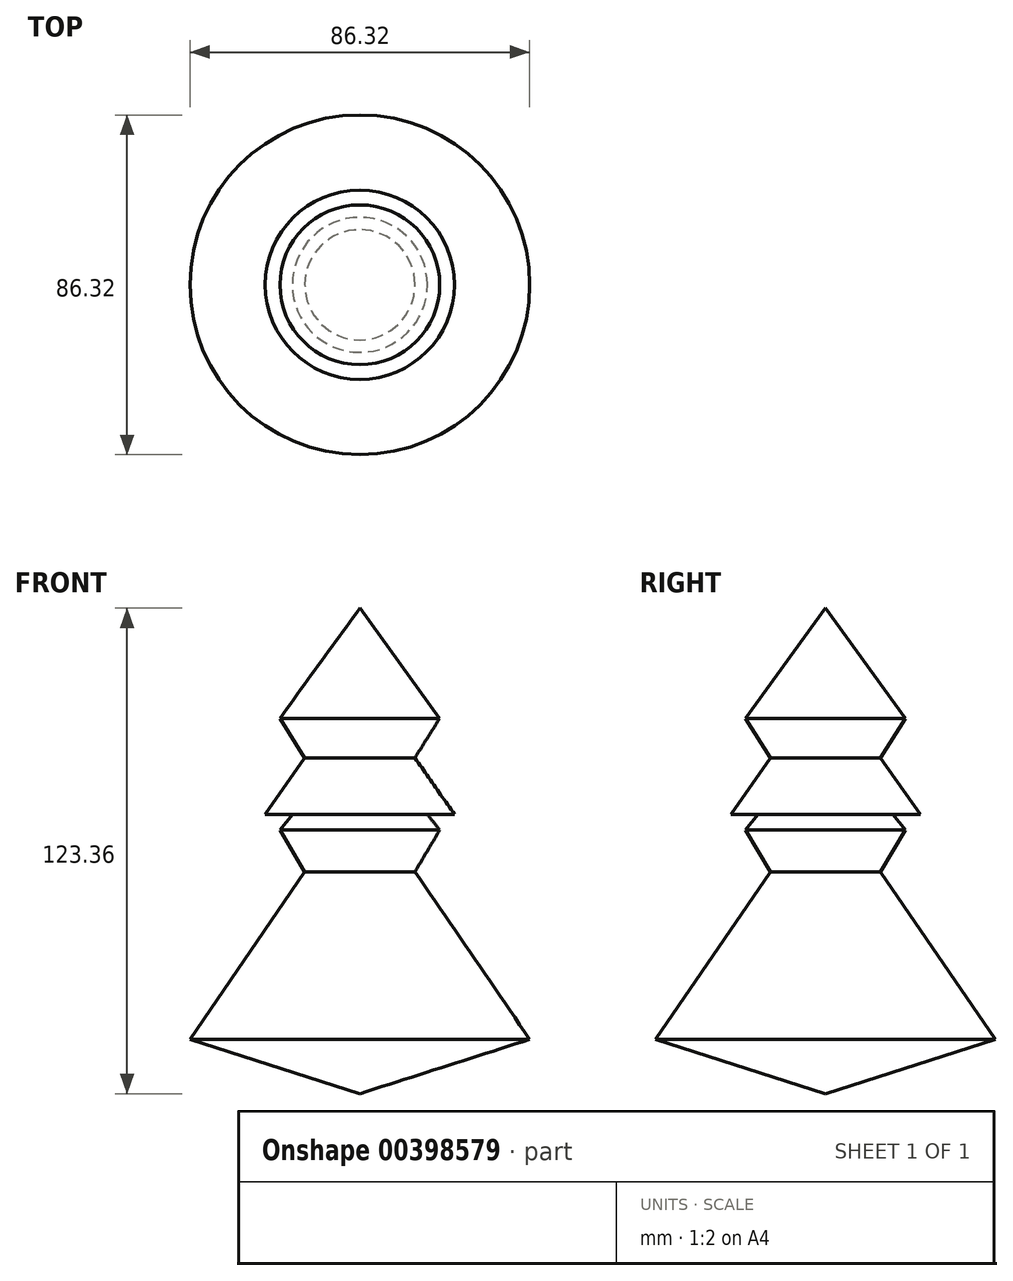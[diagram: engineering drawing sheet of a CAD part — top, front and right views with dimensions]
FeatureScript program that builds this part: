
annotation { "Feature Type Name" : "Feature", "Feature Type Description" : "" }
export const myFeature = defineFeature(function(context is Context, id is Id, definition is map)
    precondition{}
    {
        {
            var Q0;
            Q0=qCreatedBy(makeId("Front.planeOp"),FACE);
            var sketch = newSketch(context, id + "F0", { "sketchPlane" : qUnion([Q0])});
            skLineSegment(sketch, "E0", {"start": v(-50.25, 56.36) * mm, "end": v(-50.25, -67) * mm});
            skLineSegment(sketch, "E1", {"start": v(-50.25, 56.36) * mm, "end": v(-29.95, 28.38) * mm});
            skLineSegment(sketch, "E2", {"start": v(-29.95, 28.38) * mm, "end": v(-36.26, 18.33) * mm});
            skLineSegment(sketch, "E3", {"start": v(-36.26, 18.33) * mm, "end": v(-26.21, 3.94) * mm});
            skLineSegment(sketch, "E4", {"start": v(-26.21, 3.94) * mm, "end": v(-33.1, 3.94) * mm});
            skLineSegment(sketch, "E5", {"start": v(-33.1, 3.94) * mm, "end": v(-29.95, 0) * mm});
            skLineSegment(sketch, "E6", {"start": v(-29.95, 0) * mm, "end": v(-36.26, -10.64) * mm});
            skLineSegment(sketch, "E7", {"start": v(-36.26, -10.64) * mm, "end": v(-7.1, -53.2) * mm});
            skLineSegment(sketch, "E8", {"start": v(-7.1, -53.2) * mm, "end": v(-50.25, -67) * mm});
            skSolve(sketch);
        }
        {
            var Q0;
            Q0=makeQuery(id+"F0.imprint","IMPRINT",FACE,{"disambiguationData":[TD([[makeQuery(id+"F0.imprint","IMPRINT",EDGE,{"derivedFrom":sQuery(id+"F0.wireOp",EDGE,"E0")}),1.0]])]});
            var Q1;
            Q1=sQuery(id+"F0.wireOp",EDGE,"E0");
            revolve(context, id + "F1", {"entities" : qUnion([Q0]), "axis" : qUnion([Q1]), "revolveType" : RevolveType.FULL});
        }
    });
